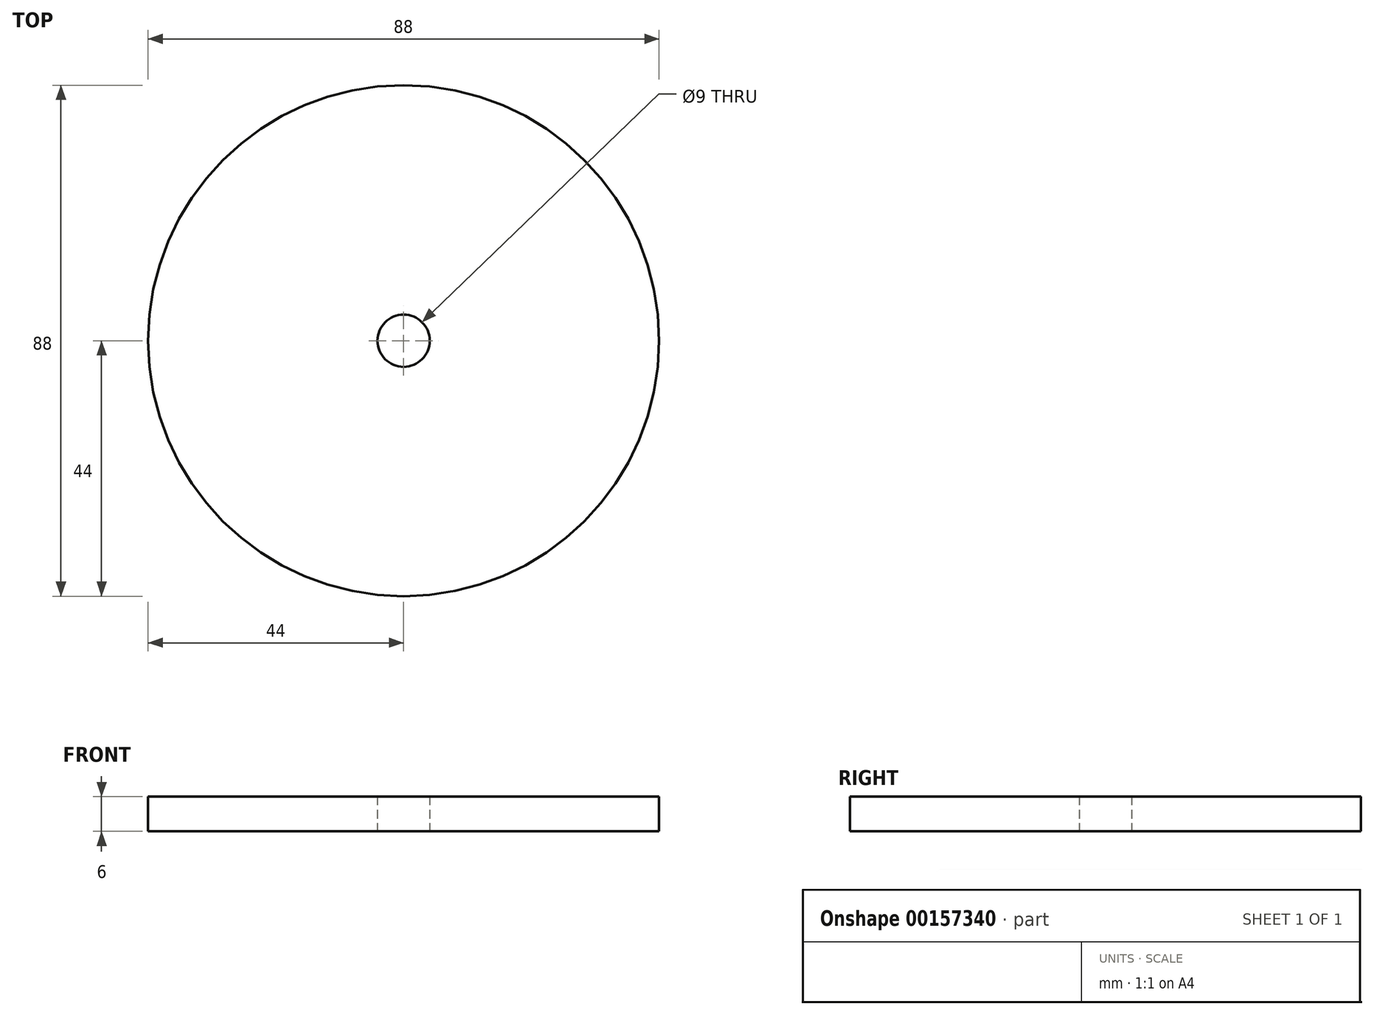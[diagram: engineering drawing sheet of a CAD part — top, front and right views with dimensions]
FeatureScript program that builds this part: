
annotation { "Feature Type Name" : "Feature", "Feature Type Description" : "" }
export const myFeature = defineFeature(function(context is Context, id is Id, definition is map)
    precondition{}
    {
        {
            var Q0;
            Q0=qCreatedBy(makeId("Top.planeOp"),FACE);
            var sketch = newSketch(context, id + "F0", { "sketchPlane" : qUnion([Q0])});
            skCircle(sketch, "E0", {"center": v(0, 0) * mm, "radius": 4.5 * mm});
            skCircle(sketch, "E1", {"center": v(0, 0) * mm, "radius": 44 * mm});
            skSolve(sketch);
        }
        {
            var Q0;
            Q0=makeQuery(id+"F0.imprint","IMPRINT",FACE,{"disambiguationData":[TD([[makeQuery(id+"F0.imprint","IMPRINT",EDGE,{"derivedFrom":sQuery(id+"F0.wireOp",EDGE,"E0")}),-1.0]])]});
            extrude(context, id + "F1", {"entities" : qUnion([Q0]), "depth" : 6 * mm});
        }
    });
